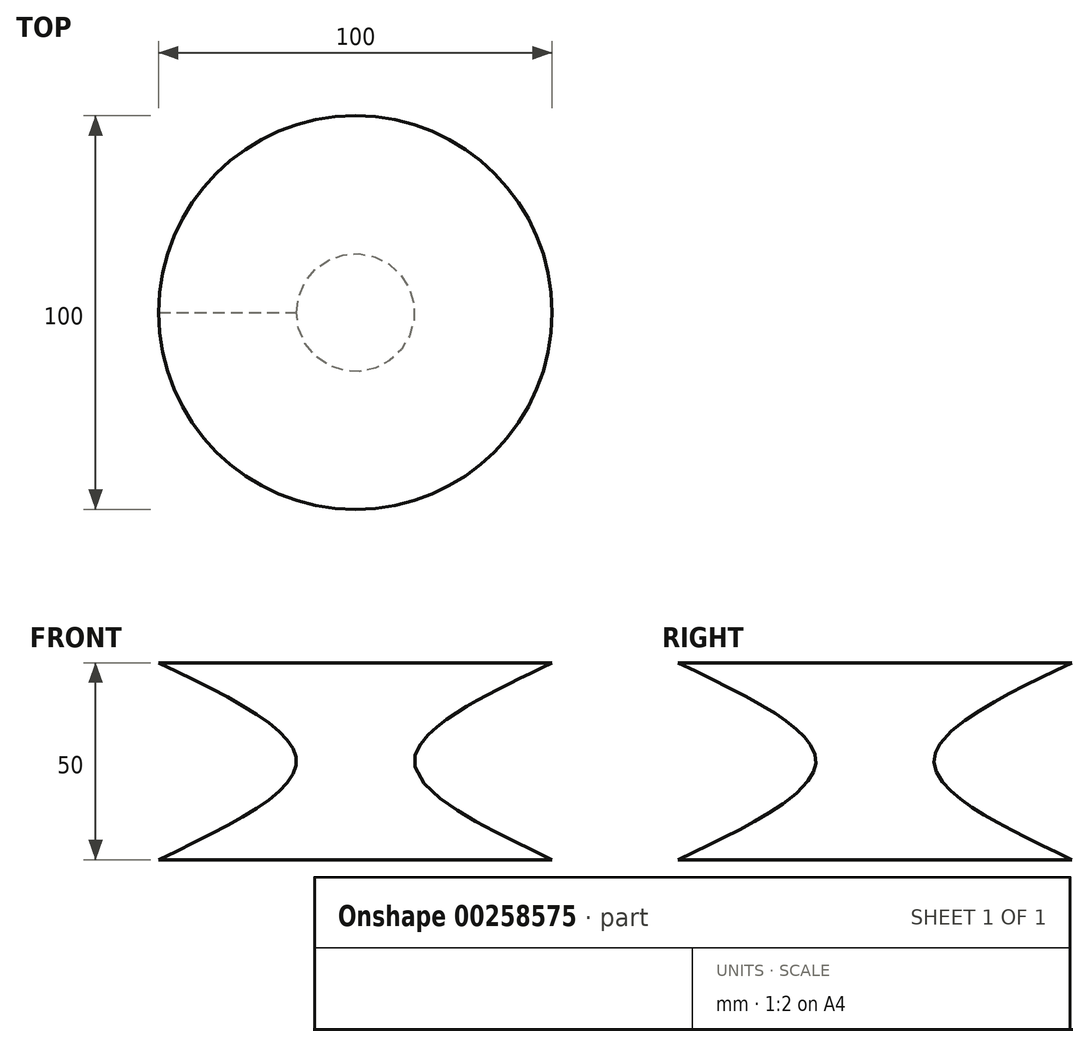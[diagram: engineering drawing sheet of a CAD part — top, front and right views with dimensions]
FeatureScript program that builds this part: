
annotation { "Feature Type Name" : "Feature", "Feature Type Description" : "" }
export const myFeature = defineFeature(function(context is Context, id is Id, definition is map)
    precondition{}
    {
        {
            var Q0;
            Q0=qCreatedBy(makeId("Top.planeOp"),FACE);
            var sketch = newSketch(context, id + "F0", { "sketchPlane" : qUnion([Q0])});
            skLineSegment(sketch, "E0.bottom", {"start": v(50, -50) * mm, "end": v(-50, -50) * mm});
            skLineSegment(sketch, "E0.top", {"start": v(50, 50) * mm, "end": v(-50, 50) * mm});
            skLineSegment(sketch, "E0.left", {"start": v(50, -50) * mm, "end": v(50, 50) * mm});
            skLineSegment(sketch, "E0.right", {"start": v(-50, -50) * mm, "end": v(-50, 50) * mm});
            skPoint(sketch, "E0.middle", {"position": v(0, 0) * mm});
            skSolve(sketch);
        }
        {
            var Q0;
            Q0=makeQuery(id+"F0.imprint","IMPRINT",FACE,{"disambiguationData":[TD([[makeQuery(id+"F0.imprint","IMPRINT",EDGE,{"derivedFrom":sQuery(id+"F0.wireOp",EDGE,"E0.bottom")}),-1.0]])]});
            extrude(context, id + "F1", {"entities" : qUnion([Q0]), "depth" : 25 * mm});
        }
        {
            var Q0;
            Q0=makeQuery(id+"F1.opExtrude","CAP_FACE",FACE,{"disambiguationData":[OSD([sQuery(id+"F0.wireOp",EDGE,"E0.bottom"),sQuery(id+"F0.wireOp",EDGE,"E0.top"),sQuery(id+"F0.wireOp",EDGE,"E0.left"),sQuery(id+"F0.wireOp",EDGE,"E0.right")])],"isStart":true});
            var sketch = newSketch(context, id + "F2", { "sketchPlane" : qUnion([Q0])});
            skCircle(sketch, "E1", {"center": v(0, 0) * mm, "radius": 50 * mm});
            skSolve(sketch);
        }
        {
            var Q0;
            Q0=makeQuery(id+"F1.opExtrude","CAP_FACE",FACE,{"disambiguationData":[OSD([sQuery(id+"F0.wireOp",EDGE,"E0.bottom"),sQuery(id+"F0.wireOp",EDGE,"E0.top"),sQuery(id+"F0.wireOp",EDGE,"E0.left"),sQuery(id+"F0.wireOp",EDGE,"E0.right")])],"isStart":false});
            var sketch = newSketch(context, id + "F3", { "sketchPlane" : qUnion([Q0])});
            skCircle(sketch, "E2", {"center": v(0, 0) * mm, "radius": 15 * mm});
            skSolve(sketch);
        }
        {
            var Q0;
            Q0=makeQuery(id+"F3.imprint","IMPRINT",FACE,{"disambiguationData":[TD([[makeQuery(id+"F3.imprint","IMPRINT",EDGE,{"derivedFrom":sQuery(id+"F3.wireOp",EDGE,"E2")}),-1.0]])]});
            var sketch = newSketch(context, id + "F4", { "sketchPlane" : qUnion([Q0])});
            skLineSegment(sketch, "E3.bottom", {"start": v(50, -50) * mm, "end": v(-50, -50) * mm});
            skLineSegment(sketch, "E3.top", {"start": v(50, 50) * mm, "end": v(-50, 50) * mm});
            skLineSegment(sketch, "E3.left", {"start": v(50, -50) * mm, "end": v(50, 50) * mm});
            skLineSegment(sketch, "E3.right", {"start": v(-50, -50) * mm, "end": v(-50, 50) * mm});
            skPoint(sketch, "E3.middle", {"position": v(0, 0) * mm});
            skSolve(sketch);
        }
        {
            var Q0;
            Q0 = qSketchRegion(id + "F4", true);
            extrude(context, id + "F5", {"entities" : qUnion([Q0]), "operationType" : NewBodyOperationType.ADD, "depth" : 25 * mm});
        }
        {
            var Q0;
            Q0=makeQuery(id+"F5.opExtrude","CAP_FACE",FACE,{"disambiguationData":[OSD([sQuery(id+"F4.wireOp",EDGE,"E3.bottom"),sQuery(id+"F4.wireOp",EDGE,"E3.top"),sQuery(id+"F4.wireOp",EDGE,"E3.left"),sQuery(id+"F4.wireOp",EDGE,"E3.right")])],"isStart":false});
            var sketch = newSketch(context, id + "F6", { "sketchPlane" : qUnion([Q0])});
            skCircle(sketch, "E4", {"center": v(0, 0) * mm, "radius": 50 * mm});
            skSolve(sketch);
        }
        {
            var Q1;
            Q1 = qSketchRegion(id + "F2", true);
            var Q2;
            Q2 = qSketchRegion(id + "F3", true);
            var Q3;
            Q3 = qSketchRegion(id + "F6", true);
            loft(context, id + "F7", {"operationType" : NewBodyOperationType.INTERSECT, "sheetProfilesArray" : [{ "sheetProfileEntities" : qUnion([Q1]) }, { "sheetProfileEntities" : qUnion([Q2]) }, { "sheetProfileEntities" : qUnion([Q3]) }]});
        }
    });
